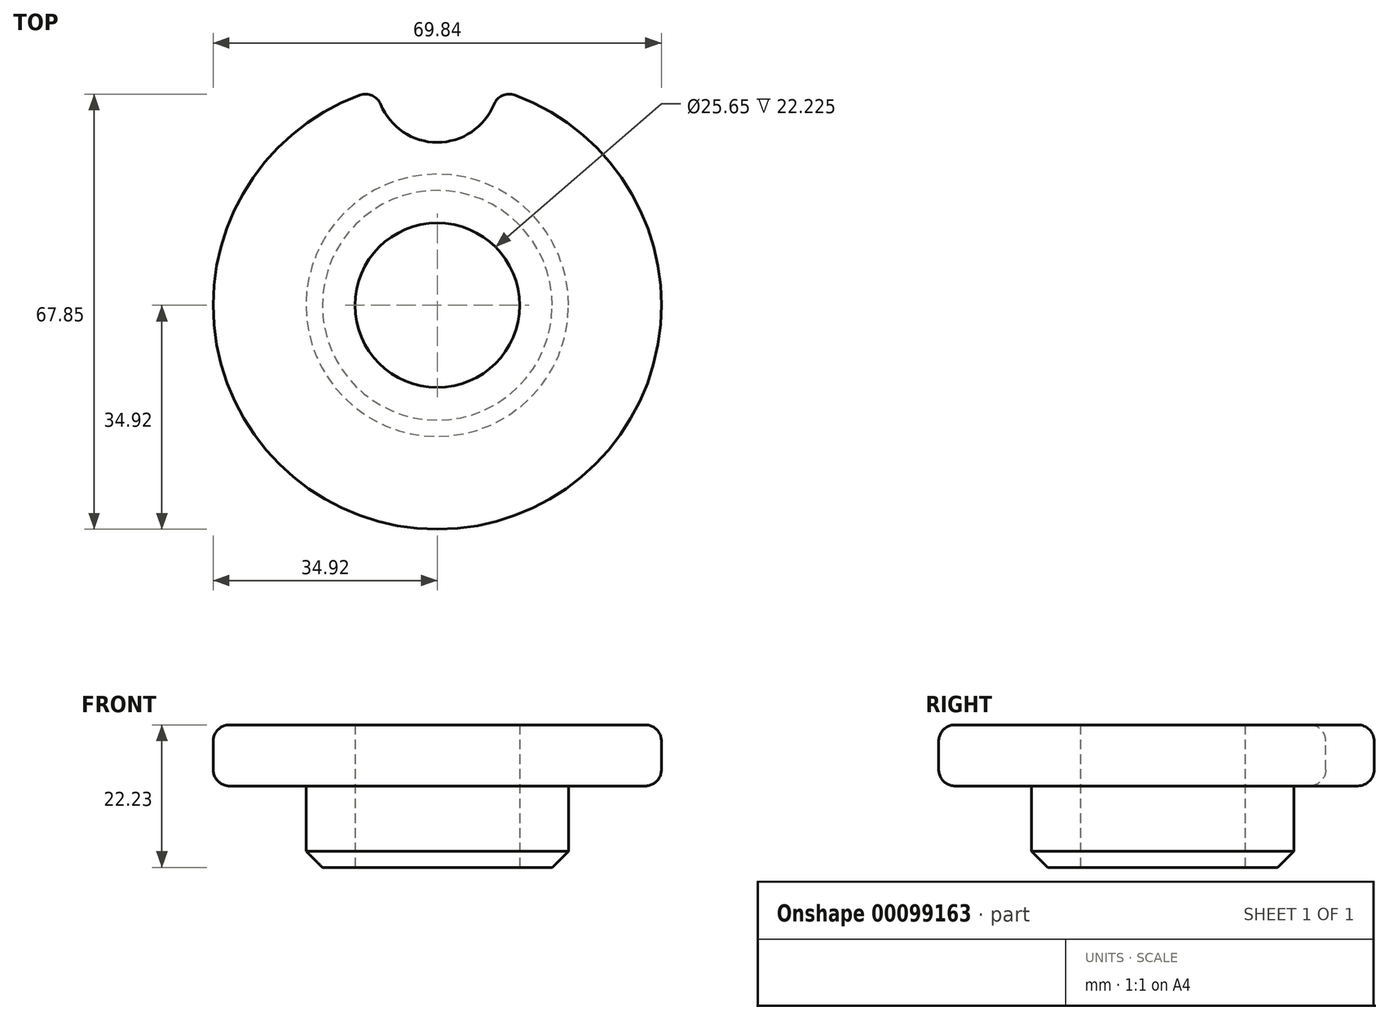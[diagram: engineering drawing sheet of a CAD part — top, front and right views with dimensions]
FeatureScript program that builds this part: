
annotation { "Feature Type Name" : "Feature", "Feature Type Description" : "" }
export const myFeature = defineFeature(function(context is Context, id is Id, definition is map)
    precondition{}
    {
        {
            var Q0;
            Q0=qCreatedBy(makeId("Front.planeOp"),FACE);
            var sketch = newSketch(context, id + "F0", { "sketchPlane" : qUnion([Q0])});
            skLineSegment(sketch, "E0", {"start": v(12.83, 0) * mm, "end": v(12.83, 22.23) * mm});
            skLineSegment(sketch, "E1", {"start": v(12.83, 22.23) * mm, "end": v(34.93, 22.23) * mm});
            skLineSegment(sketch, "E2", {"start": v(12.83, 0) * mm, "end": v(20.45, 0) * mm});
            skLineSegment(sketch, "E3", {"start": v(20.45, 0) * mm, "end": v(20.45, 12.7) * mm});
            skLineSegment(sketch, "E4", {"start": v(20.45, 12.7) * mm, "end": v(34.93, 12.7) * mm});
            skLineSegment(sketch, "E5", {"start": v(0, 0) * mm, "end": v(0, 31.2) * mm, "construction": true});
            skLineSegment(sketch, "E6", {"start": v(34.93, 12.7) * mm, "end": v(34.93, 22.23) * mm});
            skSolve(sketch);
        }
        {
            var Q0;
            Q0=qSketchRegion(id+"F0",true);
            var Q1;
            Q1=sQuery(id+"F0.wireOp",EDGE,"E5");
            revolve(context, id + "F1", {"entities" : qUnion([Q0]), "axis" : qUnion([Q1]), "revolveType" : RevolveType.FULL});
        }
        {
            var Q0;
            Q0=makeQuery(id+"F1.opRevolve","SWEPT_EDGE",EDGE,{"disambiguationData":[OSD([sQuery(id+"F0.wireOp",EDGE,"E2"),sQuery(id+"F0.wireOp",EDGE,"E3")])]});
            chamfer(context, id + "F2", {"entities" : qUnion([Q0]), "width" : 2.54 * mm, "tangentPropagation" : true});
        }
        {
            var Q0;
            Q0=makeQuery(id+"F1.opRevolve","SWEPT_FACE",FACE,{"disambiguationData":[OSD([sQuery(id+"F0.wireOp",EDGE,"E1")])]});
            var sketch = newSketch(context, id + "F3", { "sketchPlane" : qUnion([Q0])});
            skCircle(sketch, "E7", {"center": v(0, 34.93) * mm, "radius": 9.53 * mm});
            skSolve(sketch);
        }
        {
            var Q0;
            Q0=qSketchRegion(id+"F3",true);
            extrude(context, id + "F4", {"entities" : qUnion([Q0]), "operationType" : NewBodyOperationType.REMOVE, "endBound" : BoundingType.THROUGH_ALL, "oppositeDirection" : true, "depth" : 25.4 * mm});
        }
        {
            var Q0;
            Q0=makeQuery(id+"F4.boolean.opBoolean","INTERSECT",EDGE,{"disambiguationData":[OD(1.0)],"derivedFrom":[makeQuery(id+"F1.opRevolve","SWEPT_FACE",FACE,{"disambiguationData":[OSD([sQuery(id+"F0.wireOp",EDGE,"E6")])]}),makeQuery(id+"F4.opExtrude","SWEPT_FACE",FACE,{"disambiguationData":[OSD([sQuery(id+"F3.wireOp",EDGE,"E7")])]})]});
            var Q1;
            Q1=makeQuery(id+"F4.boolean.opBoolean","INTERSECT",EDGE,{"disambiguationData":[OD(0.0)],"derivedFrom":[makeQuery(id+"F1.opRevolve","SWEPT_FACE",FACE,{"disambiguationData":[OSD([sQuery(id+"F0.wireOp",EDGE,"E6")])]}),makeQuery(id+"F4.opExtrude","SWEPT_FACE",FACE,{"disambiguationData":[OSD([sQuery(id+"F3.wireOp",EDGE,"E7")])]})]});
            fillet(context, id + "F5", {"entities" : qUnion([Q0, Q1]), "radius" : 2.54 * mm, "tangentPropagation" : true, "allowEdgeOverflow" : false});
        }
        {
            var Q0;
            {var subQ0=sQuery(id+"F0.wireOp",EDGE,"E1");var subQ2=sQuery(id+"F0.wireOp",EDGE,"E6");var subQ3=makeQuery(id+"F1.opRevolve","SWEPT_FACE",FACE,{"disambiguationData":[OSD([subQ2])]});var subQ4=sQuery(id+"F3.wireOp",EDGE,"E7");var subQ5=makeQuery(id+"F5.opFillet","BLEND_FACE",FACE,{"disambiguationData":[OSD([subQ2,subQ4]),TDD([makeQuery(id+"F4.boolean.opBoolean","INTERSECT",EDGE,{"disambiguationData":[OD(1.0)],"derivedFrom":[subQ3,makeQuery(id+"F4.opExtrude","SWEPT_FACE",FACE,{"disambiguationData":[OSD([subQ4])]})]})])]});Q0=makeQuery(id+"Fep6osTPxKcJerf_1.5.F4.boolean.opBoolean","SPLIT",EDGE,{"disambiguationData":[TD([subQ5])],"derivedFrom":makeQuery(id+"Fep6osTPxKcJerf_1.4.F4.boolean.opBoolean","SPLIT",EDGE,{"disambiguationData":[TD([subQ5])],"derivedFrom":makeQuery(id+"Fep6osTPxKcJerf_1.3.F4.boolean.opBoolean","SPLIT",EDGE,{"disambiguationData":[TD([subQ5])],"derivedFrom":makeQuery(id+"Fep6osTPxKcJerf_1.2.F4.boolean.opBoolean","SPLIT",EDGE,{"disambiguationData":[TD([subQ5])],"derivedFrom":makeQuery(id+"Fep6osTPxKcJerf_1.1.F4.boolean.opBoolean","SPLIT",EDGE,{"disambiguationData":[TD([subQ5])],"derivedFrom":makeQuery(id+"F1.opRevolve","SWEPT_EDGE",EDGE,{"disambiguationData":[OSD([subQ0,subQ2])]})})})})})});}
            var Q1;
            {var subQ0=sQuery(id+"F0.wireOp",EDGE,"E4");var subQ2=sQuery(id+"F0.wireOp",EDGE,"E6");var subQ3=makeQuery(id+"F1.opRevolve","SWEPT_FACE",FACE,{"disambiguationData":[OSD([subQ2])]});var subQ4=sQuery(id+"F3.wireOp",EDGE,"E7");var subQ5=makeQuery(id+"F5.opFillet","BLEND_FACE",FACE,{"disambiguationData":[OSD([subQ2,subQ4]),TDD([makeQuery(id+"F4.boolean.opBoolean","INTERSECT",EDGE,{"disambiguationData":[OD(1.0)],"derivedFrom":[subQ3,makeQuery(id+"F4.opExtrude","SWEPT_FACE",FACE,{"disambiguationData":[OSD([subQ4])]})]})])]});Q1=makeQuery(id+"Fep6osTPxKcJerf_1.5.F4.boolean.opBoolean","SPLIT",EDGE,{"disambiguationData":[TD([subQ5])],"derivedFrom":makeQuery(id+"Fep6osTPxKcJerf_1.4.F4.boolean.opBoolean","SPLIT",EDGE,{"disambiguationData":[TD([subQ5])],"derivedFrom":makeQuery(id+"Fep6osTPxKcJerf_1.3.F4.boolean.opBoolean","SPLIT",EDGE,{"disambiguationData":[TD([subQ5])],"derivedFrom":makeQuery(id+"Fep6osTPxKcJerf_1.2.F4.boolean.opBoolean","SPLIT",EDGE,{"disambiguationData":[TD([subQ5])],"derivedFrom":makeQuery(id+"Fep6osTPxKcJerf_1.1.F4.boolean.opBoolean","SPLIT",EDGE,{"disambiguationData":[TD([subQ5])],"derivedFrom":makeQuery(id+"F1.opRevolve","SWEPT_EDGE",EDGE,{"disambiguationData":[OSD([subQ0,subQ2])]})})})})})});}
            fillet(context, id + "F6", {"entities" : qUnion([Q0, Q1]), "radius" : 2.54 * mm, "tangentPropagation" : true, "allowEdgeOverflow" : false});
        }
    });
